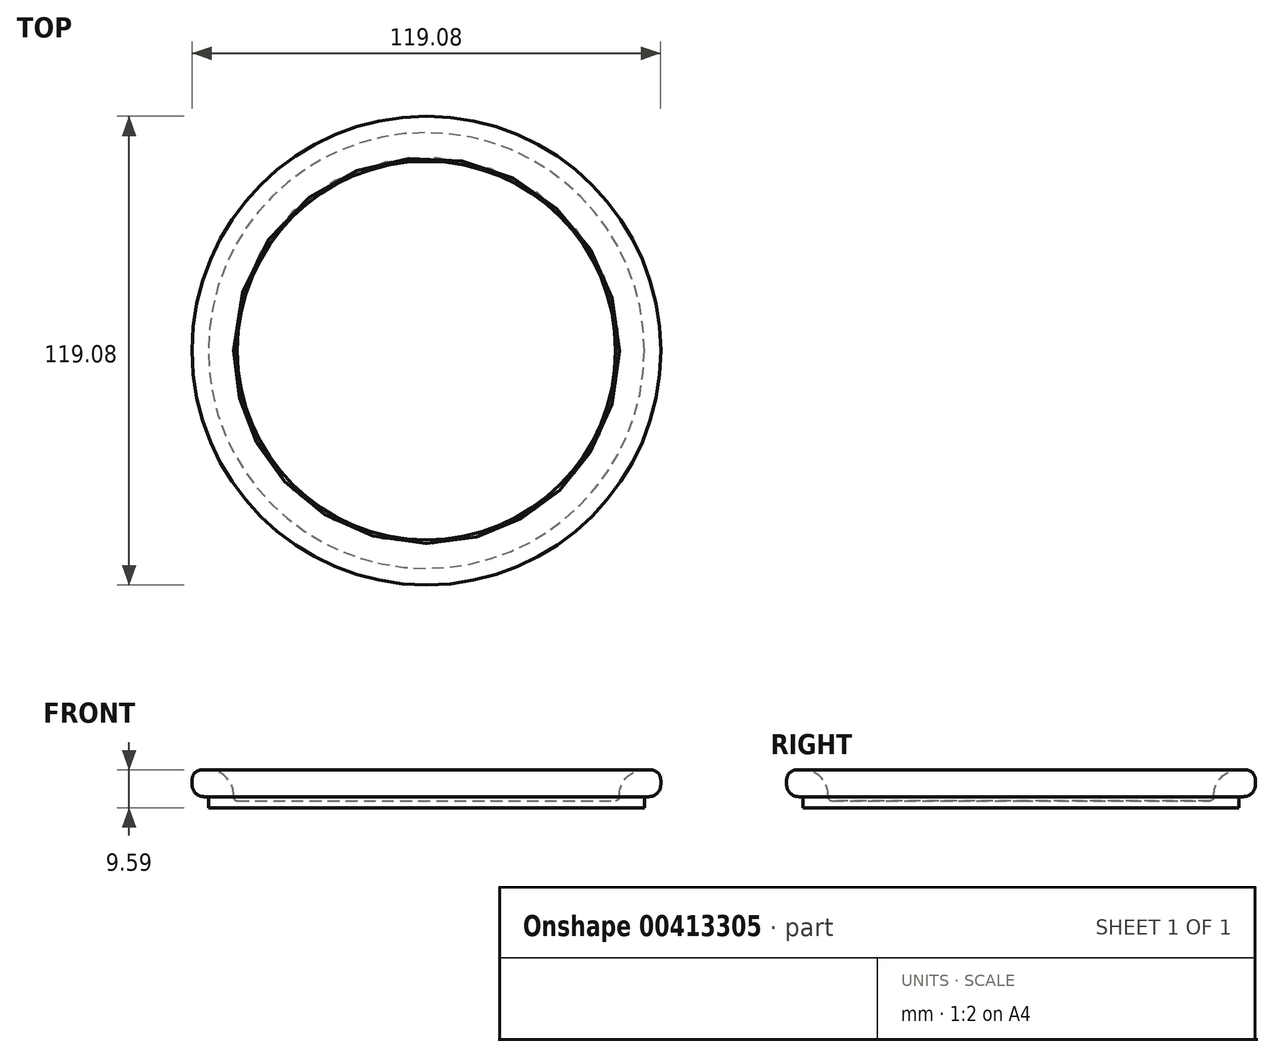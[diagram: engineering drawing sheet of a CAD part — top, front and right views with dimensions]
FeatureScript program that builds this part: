
annotation { "Feature Type Name" : "Feature", "Feature Type Description" : "" }
export const myFeature = defineFeature(function(context is Context, id is Id, definition is map)
    precondition{}
    {
        {
            var Q0;
            Q0=qCreatedBy(makeId("Front.planeOp"),FACE);
            var sketch = newSketch(context, id + "F0", { "sketchPlane" : qUnion([Q0])});
            skLineSegment(sketch, "E0", {"start": v(0, 0) * mm, "end": v(55.36, 0) * mm});
            skLineSegment(sketch, "E1", {"start": v(55.36, 0) * mm, "end": v(55.36, 2.29) * mm});
            skLineSegment(sketch, "E2", {"start": v(55.87, 2.8) * mm, "end": v(56.5, 2.8) * mm});
            skLineSegment(sketch, "E3", {"start": v(59.54, 5.84) * mm, "end": v(59.54, 7.05) * mm});
            skLineSegment(sketch, "E4", {"start": v(57, 9.59) * mm, "end": v(55.36, 9.59) * mm});
            skPoint(sketch, "E5.visualSharp", {"position": v(59.54, 9.59) * mm});
            skArc(sketch, "E5.filletArc", {"start": v(59.54, 7.05) * mm, "mid": v(58.8, 8.84) * mm, "end": v(57, 9.59) * mm});
            skPoint(sketch, "E6.visualSharp", {"position": v(59.54, 2.8) * mm});
            skArc(sketch, "E6.filletArc", {"start": v(56.5, 2.8) * mm, "mid": v(58.65, 3.69) * mm, "end": v(59.54, 5.84) * mm});
            skPoint(sketch, "E7.visualSharp", {"position": v(55.36, 2.8) * mm});
            skArc(sketch, "E7.filletArc", {"start": v(55.87, 2.8) * mm, "mid": v(55.5, 2.65) * mm, "end": v(55.36, 2.29) * mm});
            skArc(sketch, "E8", {"start": v(55.36, 9.59) * mm, "mid": v(50.72, 7.57) * mm, "end": v(49.02, 2.8) * mm});
            skArc(sketch, "E9", {"start": v(49.02, 2.8) * mm, "mid": v(48.78, 2.07) * mm, "end": v(48.08, 1.75) * mm});
            skLineSegment(sketch, "E10", {"start": v(48.08, 1.75) * mm, "end": v(0, 1.75) * mm});
            skLineSegment(sketch, "E11", {"start": v(0, 0) * mm, "end": v(0, 1.75) * mm});
            skSolve(sketch);
        }
        {
            var Q0;
            Q0 = qSketchRegion(id + "F0", true);
            var Q1;
            Q1=sQuery(id+"F0.wireOp",EDGE,"E11");
            revolve(context, id + "F1", {"entities" : qUnion([Q0]), "axis" : qUnion([Q1]), "revolveType" : RevolveType.FULL});
        }
    });
